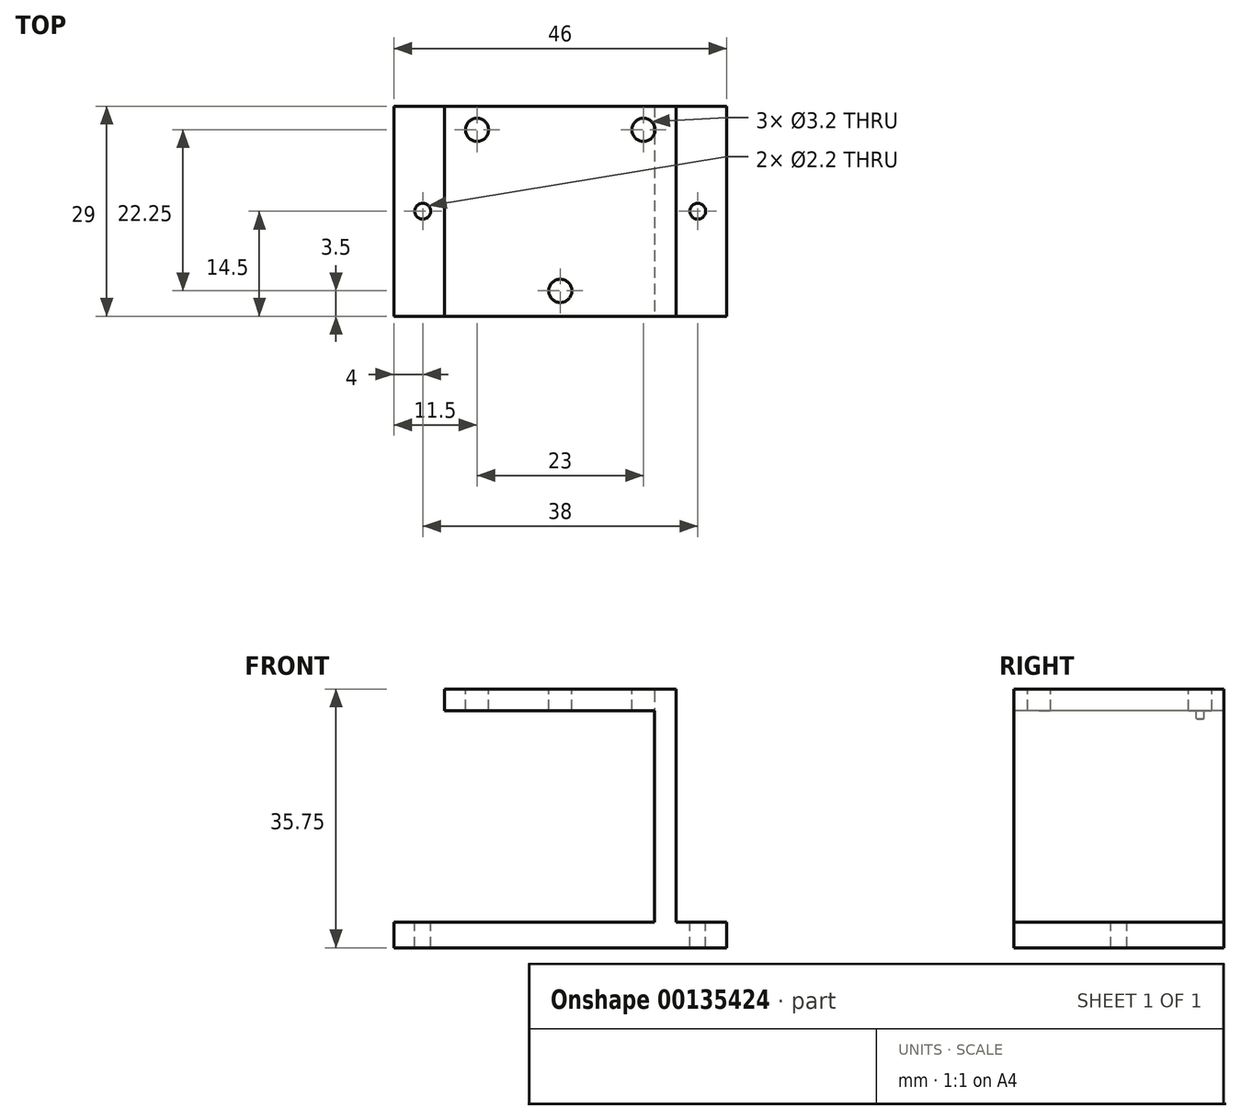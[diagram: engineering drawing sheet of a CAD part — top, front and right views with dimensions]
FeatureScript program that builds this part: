
annotation { "Feature Type Name" : "Feature", "Feature Type Description" : "" }
export const myFeature = defineFeature(function(context is Context, id is Id, definition is map)
    precondition{}
    {
        {
            var Q0;
            Q0=qCreatedBy(makeId("Top.planeOp"),FACE);
            var sketch = newSketch(context, id + "F0", { "sketchPlane" : qUnion([Q0])});
            skLineSegment(sketch, "E0.bottom", {"start": v(23, 14.5) * mm, "end": v(-23, 14.5) * mm});
            skLineSegment(sketch, "E0.top", {"start": v(23, -14.5) * mm, "end": v(-23, -14.5) * mm});
            skLineSegment(sketch, "E0.left", {"start": v(23, 14.5) * mm, "end": v(23, -14.5) * mm});
            skLineSegment(sketch, "E0.right", {"start": v(-23, 14.5) * mm, "end": v(-23, -14.5) * mm});
            skPoint(sketch, "E0.middle", {"position": v(0, 0) * mm});
            skSolve(sketch);
        }
        {
            var Q0;
            Q0 = qSketchRegion(id + "F0", true);
            extrude(context, id + "F1", {"entities" : qUnion([Q0]), "depth" : 3.5 * mm});
        }
        {
            var Q0;
            Q0=makeQuery(id+"F1.opExtrude","CAP_FACE",FACE,{"disambiguationData":[OSD([sQuery(id+"F0.wireOp",EDGE,"E0.bottom"),sQuery(id+"F0.wireOp",EDGE,"E0.top"),sQuery(id+"F0.wireOp",EDGE,"E0.left"),sQuery(id+"F0.wireOp",EDGE,"E0.right")])],"isStart":false});
            var sketch = newSketch(context, id + "F2", { "sketchPlane" : qUnion([Q0])});
            skLineSegment(sketch, "E1.bottom", {"start": v(16, -14.5) * mm, "end": v(-16, -14.5) * mm});
            skLineSegment(sketch, "E1.top", {"start": v(16, 14.5) * mm, "end": v(-16, 14.5) * mm});
            skLineSegment(sketch, "E1.left", {"start": v(16, -14.5) * mm, "end": v(16, 14.5) * mm});
            skLineSegment(sketch, "E1.right", {"start": v(-16, -14.5) * mm, "end": v(-16, 14.5) * mm});
            skPoint(sketch, "E1.middle", {"position": v(0, 0) * mm});
            skSolve(sketch);
        }
        {
            var Q0;
            Q0 = qSketchRegion(id + "F2", true);
            extrude(context, id + "F3", {"entities" : qUnion([Q0]), "operationType" : NewBodyOperationType.ADD, "depth" : 32.25 * mm});
        }
        {
            var Q0;
            Q0=makeQuery(id+"F3.boolean.opBoolean","MERGE",FACE,{"derivedFrom":[makeQuery(id+"F1.opExtrude","SWEPT_FACE",FACE,{"disambiguationData":[OSD([sQuery(id+"F0.wireOp",EDGE,"E0.top")])]}),makeQuery(id+"F3.opExtrude","SWEPT_FACE",FACE,{"disambiguationData":[OSD([sQuery(id+"F2.wireOp",EDGE,"E1.bottom")])]})]});
            var sketch = newSketch(context, id + "F4", { "sketchPlane" : qUnion([Q0])});
            skLineSegment(sketch, "E2.bottom", {"start": v(-16, 32.75) * mm, "end": v(13, 32.75) * mm});
            skLineSegment(sketch, "E2.top", {"start": v(-16, 3.5) * mm, "end": v(13, 3.5) * mm});
            skLineSegment(sketch, "E2.left", {"start": v(-16, 32.75) * mm, "end": v(-16, 3.5) * mm});
            skLineSegment(sketch, "E2.right", {"start": v(13, 32.75) * mm, "end": v(13, 3.5) * mm});
            skSolve(sketch);
        }
        {
            var Q0;
            Q0 = qSketchRegion(id + "F4", true);
            extrude(context, id + "F5", {"entities" : qUnion([Q0]), "operationType" : NewBodyOperationType.REMOVE, "oppositeDirection" : true, "depth" : 29 * mm});
        }
        {
            var Q0;
            Q0=makeQuery(id+"F3.opExtrude","CAP_FACE",FACE,{"disambiguationData":[OSD([sQuery(id+"F2.wireOp",EDGE,"E1.bottom"),sQuery(id+"F2.wireOp",EDGE,"E1.top"),sQuery(id+"F2.wireOp",EDGE,"E1.left"),sQuery(id+"F2.wireOp",EDGE,"E1.right")])],"isStart":false});
            var sketch = newSketch(context, id + "F6", { "sketchPlane" : qUnion([Q0])});
            skPoint(sketch, "E3", {"position": v(11.5, 11.25) * mm});
            skPoint(sketch, "E4", {"position": v(0, -11) * mm});
            skPoint(sketch, "E5.MirrorP", {"position": v(-11.5, 11.25) * mm});
            skSolve(sketch);
        }
        {
            var Q0;
            Q0=sQuery(id+"F6.wireOp",VERTEX,"E5.MirrorP");
            var Q1;
            Q1=sQuery(id+"F6.wireOp",VERTEX,"E3");
            var Q2;
            Q2=sQuery(id+"F6.wireOp",VERTEX,"E4");
            var Q3;
            Q3=makeQuery(id+"F1.opExtrude","SWEPT_BODY",BODY,{"disambiguationData":[OSD([sQuery(id+"F0.wireOp",EDGE,"E0.bottom"),sQuery(id+"F0.wireOp",EDGE,"E0.top"),sQuery(id+"F0.wireOp",EDGE,"E0.left"),sQuery(id+"F0.wireOp",EDGE,"E0.right")])]});
            hole(context, id + "F7", {"style" : HoleStyle.SIMPLE, "endStyle" : HoleEndStyle.BLIND, "holeDiameter" : 3.2 * mm, "holeDepth" : 4.1 * mm, "locations" : qUnion([Q0, Q1, Q2]), "scope" : qUnion([Q3])});
        }
        {
            var Q0;
            {var subQ0=sQuery(id+"F0.wireOp",EDGE,"E0.left");var subQ1=sQuery(id+"F0.wireOp",EDGE,"E0.top");var subQ2=sQuery(id+"F0.wireOp",EDGE,"E0.bottom");Q0=makeQuery(id+"F3.boolean.opBoolean","SPLIT",FACE,{"disambiguationData":[TD([makeQuery(id+"F1.opExtrude","SWEPT_FACE",FACE,{"disambiguationData":[OSD([subQ0])]})])],"derivedFrom":makeQuery(id+"F1.opExtrude","CAP_FACE",FACE,{"disambiguationData":[OSD([subQ2,subQ1,subQ0,sQuery(id+"F0.wireOp",EDGE,"E0.right")])],"isStart":false})});}
            var sketch = newSketch(context, id + "F8", { "sketchPlane" : qUnion([Q0])});
            skPoint(sketch, "E6", {"position": v(19, 0) * mm});
            skPoint(sketch, "E7.MirrorP", {"position": v(-19, 0) * mm});
            skSolve(sketch);
        }
        {
            var Q0;
            Q0=sQuery(id+"F8.wireOp",VERTEX,"E7.MirrorP");
            var Q1;
            Q1=sQuery(id+"F8.wireOp",VERTEX,"E6");
            var Q2;
            Q2=makeQuery(id+"F1.opExtrude","SWEPT_BODY",BODY,{"disambiguationData":[OSD([sQuery(id+"F0.wireOp",EDGE,"E0.bottom"),sQuery(id+"F0.wireOp",EDGE,"E0.top"),sQuery(id+"F0.wireOp",EDGE,"E0.left"),sQuery(id+"F0.wireOp",EDGE,"E0.right")])]});
            hole(context, id + "F9", {"style" : HoleStyle.SIMPLE, "endStyle" : HoleEndStyle.THROUGH, "holeDiameter" : 2.2 * mm, "locations" : qUnion([Q0, Q1]), "scope" : qUnion([Q2]), "isTappedThrough" : true});
        }
    });
